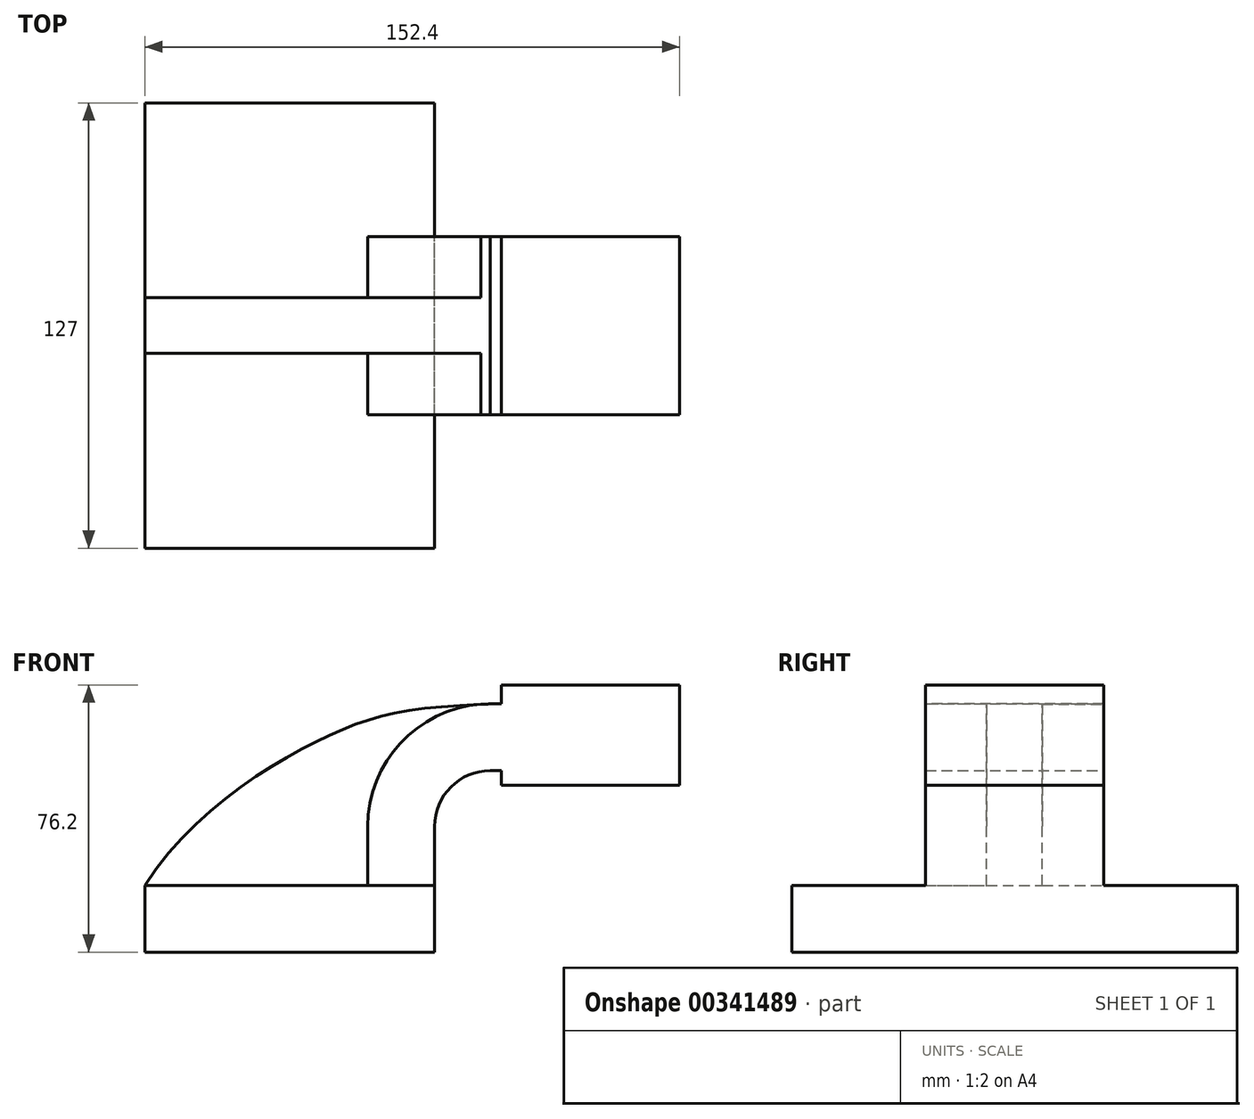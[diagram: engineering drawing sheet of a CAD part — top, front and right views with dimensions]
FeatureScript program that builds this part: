
annotation { "Feature Type Name" : "Feature", "Feature Type Description" : "" }
export const myFeature = defineFeature(function(context is Context, id is Id, definition is map)
    precondition{}
    {
        {
            var Q0;
            Q0=qCreatedBy(makeId("Front.planeOp"),FACE);
            var sketch = newSketch(context, id + "F0", { "sketchPlane" : qUnion([Q0])});
            skLineSegment(sketch, "E0.bottom", {"start": v(-41.28, -9.53) * mm, "end": v(41.28, -9.53) * mm});
            skLineSegment(sketch, "E0.top", {"start": v(-41.28, 9.53) * mm, "end": v(41.28, 9.53) * mm});
            skLineSegment(sketch, "E0.left", {"start": v(-41.28, -9.53) * mm, "end": v(-41.28, 9.53) * mm});
            skLineSegment(sketch, "E0.right", {"start": v(41.28, -9.53) * mm, "end": v(41.28, 9.53) * mm});
            skPoint(sketch, "E0.middle", {"position": v(0, 0) * mm});
            skLineSegment(sketch, "E1.bottom", {"start": v(60.33, 38.1) * mm, "end": v(111.13, 38.1) * mm});
            skLineSegment(sketch, "E1.top", {"start": v(60.32, 66.67) * mm, "end": v(111.13, 66.67) * mm});
            skLineSegment(sketch, "E1.left", {"start": v(60.33, 38.1) * mm, "end": v(60.32, 66.67) * mm});
            skLineSegment(sketch, "E1.right", {"start": v(111.13, 38.1) * mm, "end": v(111.13, 66.67) * mm});
            skPoint(sketch, "E1.middle", {"position": v(85.73, 52.39) * mm});
            skLineSegment(sketch, "E2", {"start": v(41.28, 9.53) * mm, "end": v(41.28, 26.31) * mm});
            skArc(sketch, "E3", {"start": v(41.28, 26.31) * mm, "mid": v(45.92, 37.54) * mm, "end": v(57.15, 42.19) * mm});
            skLineSegment(sketch, "E4", {"start": v(57.15, 42.19) * mm, "end": v(64.74, 42.19) * mm});
            skLineSegment(sketch, "E5.0", {"start": v(57.15, 61.24) * mm, "end": v(64.74, 61.24) * mm});
            skArc(sketch, "E5.1", {"start": v(22.23, 26.31) * mm, "mid": v(32.45, 51.01) * mm, "end": v(57.15, 61.24) * mm});
            skLineSegment(sketch, "E5.2", {"start": v(22.23, 9.53) * mm, "end": v(22.23, 26.31) * mm});
            skFitSpline(sketch, "E6", {"points": [v(-41.28, 9.53) * mm, v(9.97, 51.67) * mm, v(57.15, 61.24) * mm], "startDerivative": vector(71.8, 112.74) * mm, "endDerivative": vector(152.03, 5.41) * mm});
            skSolve(sketch);
        }
        {
            var Q0;
            Q0=makeQuery(id+"F0.imprint","IMPRINT",FACE,{"disambiguationData":[TD([[makeQuery(id+"F0.imprint","IMPRINT",EDGE,{"derivedFrom":sQuery(id+"F0.wireOp",EDGE,"E0.bottom")}),1.0]])]});
            extrude(context, id + "F1", {"entities" : qUnion([Q0]), "endBound" : BoundingType.SYMMETRIC, "depth" : 127 * mm});
        }
        {
            var Q0;
            {var subQ0=sQuery(id+"F0.wireOp",EDGE,"E2");Q0=makeQuery(id+"F0.imprint","IMPRINT",FACE,{"disambiguationData":[TD([[makeQuery(id+"F0.imprint","IMPRINT",EDGE,{"derivedFrom":subQ0}),1.0]])]});}
            var Q1;
            {var subQ3=sQuery(id+"F0.wireOp",EDGE,"E1.bottom");Q1=makeQuery(id+"F0.imprint","IMPRINT",FACE,{"disambiguationData":[TD([[makeQuery(id+"F0.imprint","IMPRINT",EDGE,{"derivedFrom":subQ3}),1.0]])]});}
            extrude(context, id + "F2", {"entities" : qUnion([Q0, Q1]), "operationType" : NewBodyOperationType.ADD, "endBound" : BoundingType.SYMMETRIC, "depth" : 50.8 * mm});
        }
        {
            var Q0;
            {var subQ3=sQuery(id+"F0.wireOp",EDGE,"E5.2");Q0=makeQuery(id+"F0.imprint","IMPRINT",FACE,{"disambiguationData":[TD([[makeQuery(id+"F0.imprint","IMPRINT",EDGE,{"derivedFrom":subQ3}),1.0]])]});}
            extrude(context, id + "F3", {"entities" : qUnion([Q0]), "operationType" : NewBodyOperationType.ADD, "endBound" : BoundingType.SYMMETRIC, "depth" : 15.88 * mm});
        }
    });
